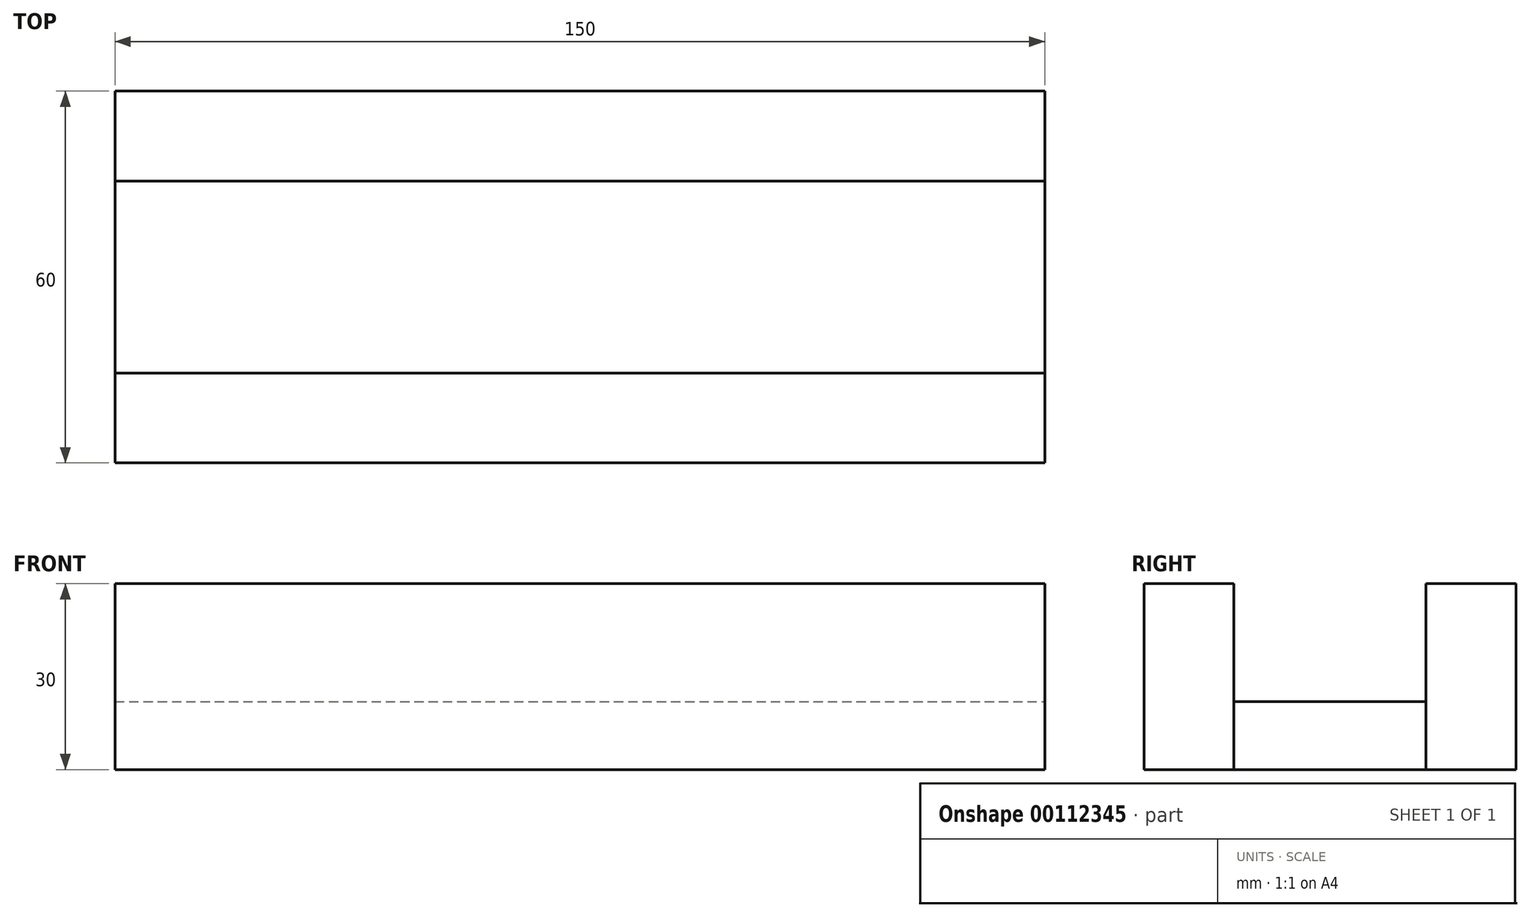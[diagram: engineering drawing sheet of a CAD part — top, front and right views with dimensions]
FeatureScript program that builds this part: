
annotation { "Feature Type Name" : "Feature", "Feature Type Description" : "" }
export const myFeature = defineFeature(function(context is Context, id is Id, definition is map)
    precondition{}
    {
        {
            var Q0;
            Q0=qCreatedBy(makeId("Top.planeOp"),FACE);
            var sketch = newSketch(context, id + "F0", { "sketchPlane" : qUnion([Q0])});
            skLineSegment(sketch, "E0.bottom", {"start": v(75, 30) * mm, "end": v(-75, 30) * mm});
            skLineSegment(sketch, "E0.top", {"start": v(75, -30) * mm, "end": v(-75, -30) * mm});
            skLineSegment(sketch, "E0.left", {"start": v(75, 30) * mm, "end": v(75, -30) * mm});
            skLineSegment(sketch, "E0.right", {"start": v(-75, 30) * mm, "end": v(-75, -30) * mm});
            skPoint(sketch, "E0.middle", {"position": v(0, 0) * mm});
            skLineSegment(sketch, "E1.bottom", {"start": v(-75, 15.5) * mm, "end": v(75, 15.5) * mm});
            skLineSegment(sketch, "E1.top", {"start": v(-75, -15.5) * mm, "end": v(75, -15.5) * mm});
            skLineSegment(sketch, "E1.left", {"start": v(-75, 15.5) * mm, "end": v(-75, -15.5) * mm});
            skLineSegment(sketch, "E1.right", {"start": v(75, 15.5) * mm, "end": v(75, -15.5) * mm});
            skSolve(sketch);
        }
        {
            var Q0;
            {var subQ0=sQuery(id+"F0.wireOp",EDGE,"E0.top");Q0=makeQuery(id+"F0.imprint","IMPRINT",FACE,{"disambiguationData":[TD([[makeQuery(id+"F0.imprint","IMPRINT",EDGE,{"derivedFrom":subQ0}),-1.0]])]});}
            var Q1;
            {var subQ0=sQuery(id+"F0.wireOp",EDGE,"E0.bottom");Q1=makeQuery(id+"F0.imprint","IMPRINT",FACE,{"disambiguationData":[TD([[makeQuery(id+"F0.imprint","IMPRINT",EDGE,{"derivedFrom":subQ0}),1.0]])]});}
            extrude(context, id + "F1", {"entities" : qUnion([Q0, Q1]), "depth" : 30 * mm});
        }
        {
            var Q0;
            Q0=makeQuery(id+"F0.imprint","IMPRINT",FACE,{"disambiguationData":[TD([[makeQuery(id+"F0.imprint","IMPRINT",EDGE,{"derivedFrom":sQuery(id+"F0.wireOp",EDGE,"E1.bottom")}),-1.0]])]});
            extrude(context, id + "F2", {"entities" : qUnion([Q0]), "depth" : 11 * mm});
        }
        {
            var Q0;
            Q0=makeQuery(id+"F0.imprint","IMPRINT",FACE,{"disambiguationData":[TD([[makeQuery(id+"F0.imprint","IMPRINT",EDGE,{"derivedFrom":sQuery(id+"F0.wireOp",EDGE,"E0.bottom")}),1.0]])]});
            extrude(context, id + "F3", {"entities" : qUnion([Q0]), "depth" : 30 * mm});
        }
    });
